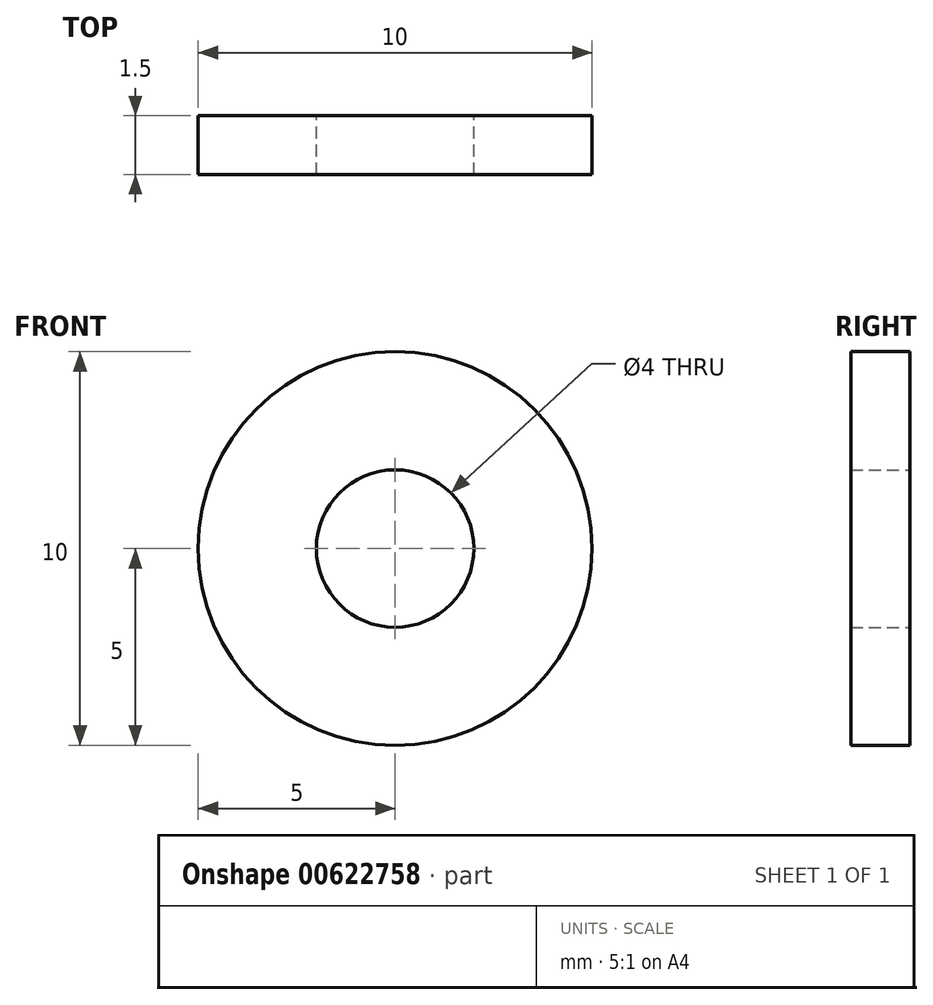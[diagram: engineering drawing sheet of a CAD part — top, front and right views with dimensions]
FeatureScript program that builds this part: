
annotation { "Feature Type Name" : "Feature", "Feature Type Description" : "" }
export const myFeature = defineFeature(function(context is Context, id is Id, definition is map)
    precondition{}
    {
        {
            var Q0;
            Q0=qCreatedBy(makeId("Front.planeOp"),FACE);
            var sketch = newSketch(context, id + "F0", { "sketchPlane" : qUnion([Q0])});
            skCircle(sketch, "E0", {"center": v(0, 0) * mm, "radius": 2 * mm});
            skCircle(sketch, "E1", {"center": v(0, 0) * mm, "radius": 5 * mm});
            skSolve(sketch);
        }
        {
            var Q0;
            Q0=makeQuery(id+"F0.imprint","IMPRINT",FACE,{"disambiguationData":[TD([[makeQuery(id+"F0.imprint","IMPRINT",EDGE,{"derivedFrom":sQuery(id+"F0.wireOp",EDGE,"E0")}),-1.0]])]});
            extrude(context, id + "F1", {"entities" : qUnion([Q0]), "depth" : 1.5 * mm, "offsetDistance" : 25.4 * mm});
        }
    });
